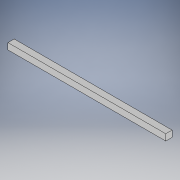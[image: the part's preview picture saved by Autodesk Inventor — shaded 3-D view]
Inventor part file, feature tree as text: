
AUTODESK INVENTOR PART (.ipt)
format: ipt  version: 2018 (Build 220112000, 112)  size: 92,160 bytes
history: native  units: in
note: dims shown in document units (in); Inventor stores cm internally (conversion verified against a paired STEP export)
features: extrude x1, sketch x1
ambient origin geometry x8: Origin, YZ Plane, XZ Plane, XY Plane, X Axis, Y Axis, Z Axis, Center Point
bodies: Solid1 (feature_tree)
feature tree (2):
  extrude  "Extrusion1"  Depth=1.0in
  sketch  "Sketch1"  dims[d0=25.0in d1=1.0in d2=1.0in d3=0.0in]
